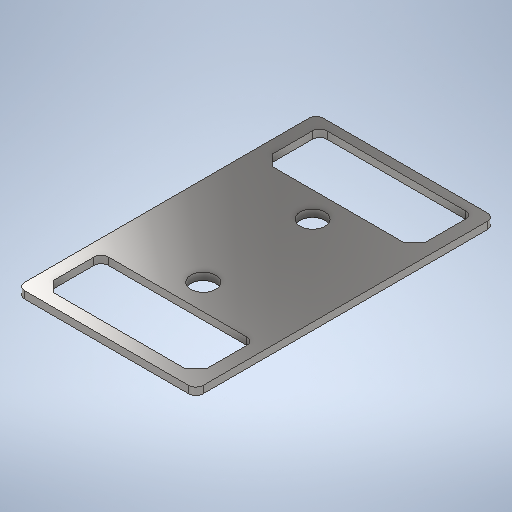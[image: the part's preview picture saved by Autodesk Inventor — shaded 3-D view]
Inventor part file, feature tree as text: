
AUTODESK INVENTOR PART (.ipt)
format: ipt  version: 2025 (Build 290162000, 162)  size: 310,272 bytes
history: native  units: mm
features: sketch x3, extrude x2, hole x1
ambient origin geometry x8: Origin, YZ Plane, XZ Plane, XY Plane, X Axis, Y Axis, Z Axis, Center Point
bodies: Solid1 (feature_tree)
feature tree (6):
  extrude  "Extrusion1"  Depth=41.0mm
  extrude  "Extrusion2"  Depth=1.0mm TaperAngle=0.0deg
  hole  "Hole1"  [1 undecoded]
  sketch  "Sketch1"  dims[d0=24.5mm d1=41.0mm]
  sketch  "Sketch2"  dims[d2=1.0mm d3=1.0mm d4=0.0mm]
  sketch  "Sketch3"  dims[d5=30.0mm d6=0.0mm d7=0.0mm d8=1.25mm d9=8.0mm d10=8.0mm d11=21.0mm d12=21.0mm d14=1.5mm d15=1.5mm d16=1.5mm d17=1.5mm d18=1.5mm d19=1.5mm d20=1.5mm d21=1.0mm d22=1.0mm d23=15.0mm d24=12.74mm d25=3.4mm d26=6.0mm d27=6.3mm d28=2.0mm d29=90.0deg d30=7.9mm d31=20.594885mm]
note: 1 required parameter value undecoded (feature->parameter linkage not recoverable at this tier; creation-order binding heuristic only, values carry confidence <= 0.55)
